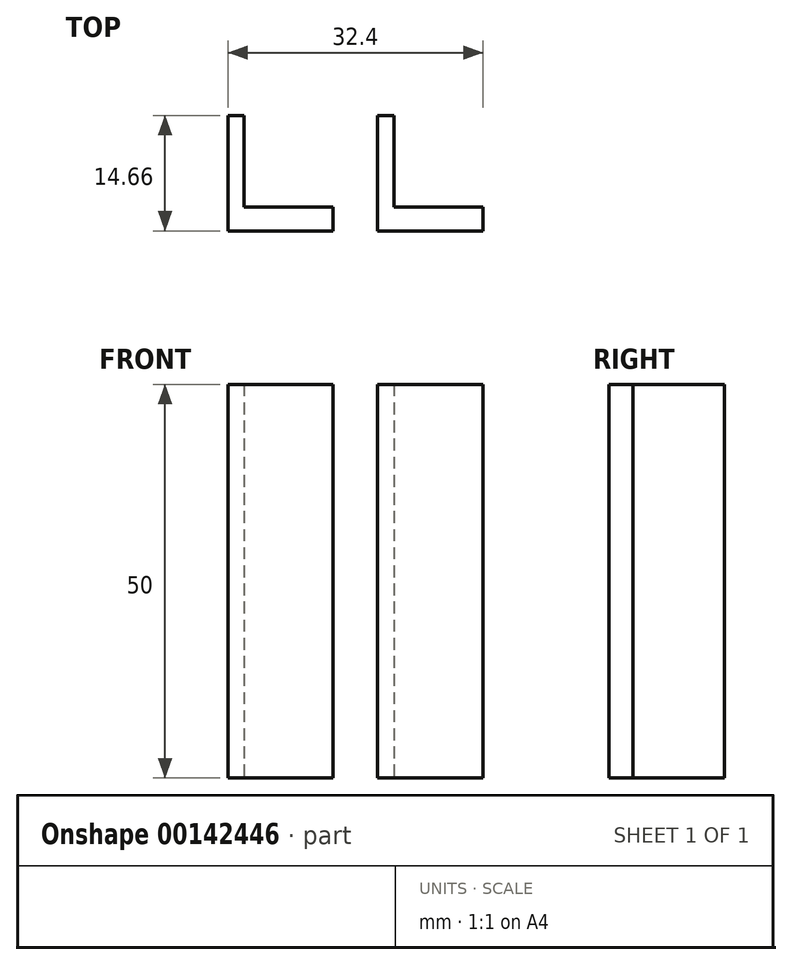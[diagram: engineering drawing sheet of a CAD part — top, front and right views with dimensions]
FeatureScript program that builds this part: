
annotation { "Feature Type Name" : "Feature", "Feature Type Description" : "" }
export const myFeature = defineFeature(function(context is Context, id is Id, definition is map)
    precondition{}
    {
        {
            var Q0;
            Q0=qCreatedBy(makeId("Top.planeOp"),FACE);
            var sketch = newSketch(context, id + "F0", { "sketchPlane" : qUnion([Q0])});
            skLineSegment(sketch, "E0", {"start": v(0, 0) * mm, "end": v(0, -14.66) * mm});
            skLineSegment(sketch, "E1", {"start": v(0, -14.66) * mm, "end": v(13.37, -14.66) * mm});
            skLineSegment(sketch, "E2", {"start": v(13.37, -14.66) * mm, "end": v(13.37, -11.62) * mm});
            skLineSegment(sketch, "E3", {"start": v(13.37, -11.62) * mm, "end": v(2.04, -11.62) * mm});
            skLineSegment(sketch, "E4", {"start": v(2.04, -11.62) * mm, "end": v(2.04, 0) * mm});
            skLineSegment(sketch, "E5", {"start": v(2.04, 0) * mm, "end": v(0, 0) * mm});
            skSolve(sketch);
        }
        {
            var Q0;
            Q0 = qSketchRegion(id + "F0", true);
            extrude(context, id + "F1", {"entities" : qUnion([Q0]), "depth" : 50 * mm});
        }
        {
            var Q0;
            Q0=makeQuery(id+"F1.opExtrude","SWEPT_BODY",BODY,{"disambiguationData":[OSD([sQuery(id+"F0.wireOp",EDGE,"E0"),sQuery(id+"F0.wireOp",EDGE,"E1"),sQuery(id+"F0.wireOp",EDGE,"E2"),sQuery(id+"F0.wireOp",EDGE,"E3"),sQuery(id+"F0.wireOp",EDGE,"E4"),sQuery(id+"F0.wireOp",EDGE,"E5")])]});
            transform(context, id + "F2", {"entities" : qUnion([Q0]), "transformType" : TransformType.TRANSLATION_3D, "dx" : 19.03 * mm, "dy" : 0 * mm, "dz" : 0 * mm, "makeCopy" : true});
        }
    });
